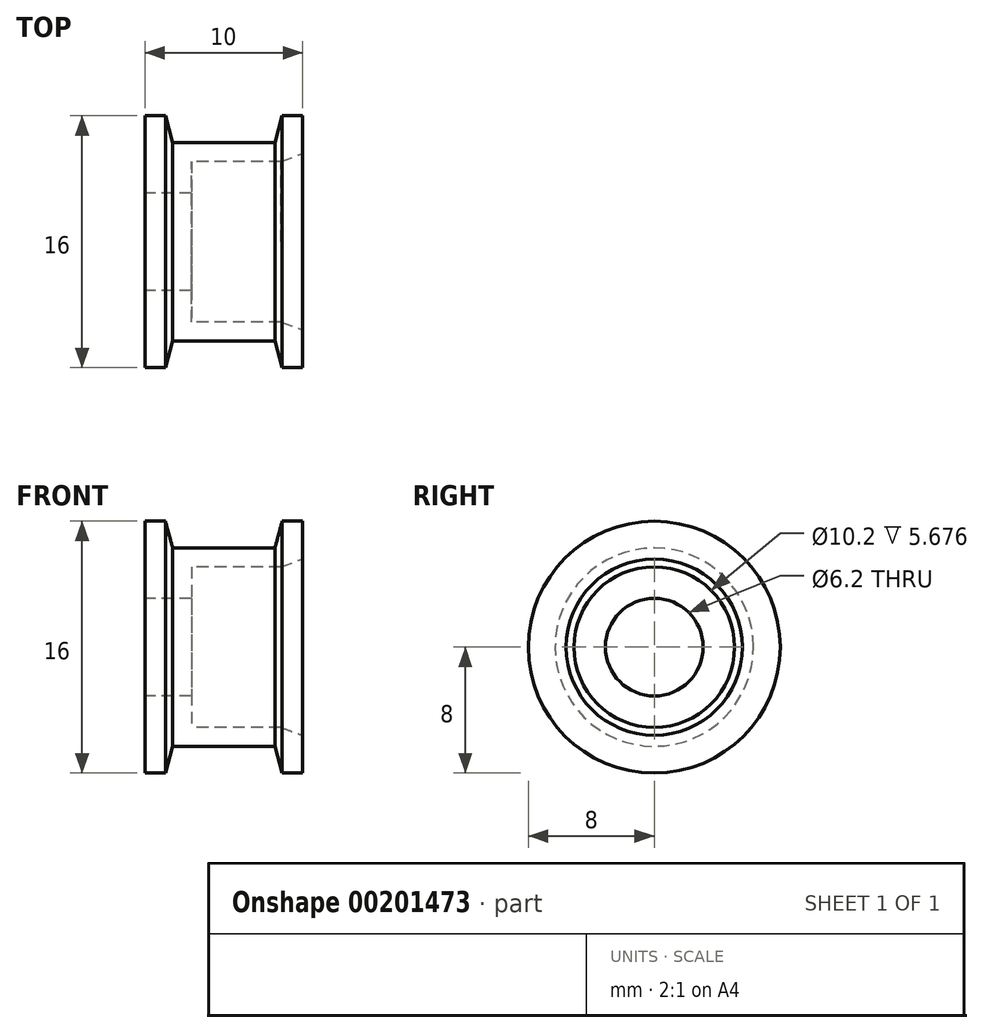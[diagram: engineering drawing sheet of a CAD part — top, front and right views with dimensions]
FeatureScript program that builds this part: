
annotation { "Feature Type Name" : "Feature", "Feature Type Description" : "" }
export const myFeature = defineFeature(function(context is Context, id is Id, definition is map)
    precondition{}
    {
        {
            var Q0;
            Q0=qCreatedBy(makeId("Front.planeOp"),FACE);
            var sketch = newSketch(context, id + "F0", { "sketchPlane" : qUnion([Q0])});
            skLineSegment(sketch, "E0", {"start": v(-2.05, 0) * mm, "end": v(2.05, 0) * mm, "construction": true});
            skLineSegment(sketch, "E1.rect.bottom", {"start": v(1.25, 5.1) * mm, "end": v(-1.25, 5.1) * mm});
            skLineSegment(sketch, "E1.rect.top", {"start": v(1.25, -5.1) * mm, "end": v(-1.25, -5.1) * mm});
            skLineSegment(sketch, "E1.rect.left", {"start": v(2.05, 4.3) * mm, "end": v(2.05, -4.3) * mm});
            skLineSegment(sketch, "E1.rect.right", {"start": v(-2.05, 5.1) * mm, "end": v(-2.05, -4.3) * mm});
            skPoint(sketch, "E1.rect.middle", {"position": v(0, 0) * mm});
            skLineSegment(sketch, "E2", {"start": v(0, 0) * mm, "end": v(0, 8) * mm, "construction": true});
            skLineSegment(sketch, "E3", {"start": v(-5, 8) * mm, "end": v(-3.7, 8) * mm});
            skLineSegment(sketch, "E4", {"start": v(-3.7, 8) * mm, "end": v(-3.25, 6.3) * mm});
            skLineSegment(sketch, "E5", {"start": v(-5, 8) * mm, "end": v(-5, 3.1) * mm});
            skLineSegment(sketch, "E6", {"start": v(-5, 3.1) * mm, "end": v(-2.05, 3.1) * mm});
            skLineSegment(sketch, "E7.0.MirrorCS", {"start": v(3.7, 8) * mm, "end": v(3.25, 6.3) * mm});
            skLineSegment(sketch, "E8.0.MirrorCS", {"start": v(5, 8) * mm, "end": v(3.7, 8) * mm});
            skLineSegment(sketch, "E9.0.MirrorCS", {"start": v(5, 8) * mm, "end": v(5, 5.1) * mm});
            skLineSegment(sketch, "E10", {"start": v(-3.25, 6.3) * mm, "end": v(3.25, 6.3) * mm});
            skLineSegment(sketch, "E11", {"start": v(-2.05, 5.1) * mm, "end": v(5, 5.1) * mm});
            skPoint(sketch, "E12.visualSharp", {"position": v(2.05, 5.1) * mm});
            skArc(sketch, "E12.filletArc", {"start": v(2.05, 4.3) * mm, "mid": v(1.82, 4.87) * mm, "end": v(1.25, 5.1) * mm});
            skPoint(sketch, "E13.visualSharp", {"position": v(-2.05, 5.1) * mm});
            skArc(sketch, "E13.filletArc", {"start": v(-1.25, 5.1) * mm, "mid": v(-1.82, 4.87) * mm, "end": v(-2.05, 4.3) * mm});
            skPoint(sketch, "E14.visualSharp", {"position": v(2.05, -5.1) * mm});
            skArc(sketch, "E14.filletArc", {"start": v(1.25, -5.1) * mm, "mid": v(1.82, -4.87) * mm, "end": v(2.05, -4.3) * mm});
            skPoint(sketch, "E15.visualSharp", {"position": v(-2.05, -5.1) * mm});
            skArc(sketch, "E15.filletArc", {"start": v(-2.05, -4.3) * mm, "mid": v(-1.82, -4.87) * mm, "end": v(-1.25, -5.1) * mm});
            skSolve(sketch);
        }
        {
            var Q0;
            Q0=makeQuery(id+"F0.imprint","IMPRINT",FACE,{"disambiguationData":[TD([[makeQuery(id+"F0.imprint","IMPRINT",EDGE,{"derivedFrom":sQuery(id+"F0.wireOp",EDGE,"E3")}),-1.0]])]});
            var Q1;
            Q1=sQuery(id+"F0.wireOp",EDGE,"E0");
            revolve(context, id + "F1", {"entities" : qUnion([Q0]), "axis" : qUnion([Q1]), "revolveType" : RevolveType.FULL});
        }
        {
            var Q0;
            Q0=makeQuery(id+"F1.opRevolve","SWEPT_EDGE",EDGE,{"disambiguationData":[OSD([sQuery(id+"F0.wireOp",EDGE,"E9.0.MirrorCS"),sQuery(id+"F0.wireOp",EDGE,"E11")])]});
            chamfer(context, id + "F2", {"entities" : qUnion([Q0]), "chamferType" : ChamferType.OFFSET_ANGLE, "width" : 0.5 * mm, "oppositeDirection" : false, "angle" : 70 * degree, "tangentPropagation" : true});
        }
    });
